# Revit family: LW3-168 MT
name_source: partatom
category: Generic Models
units: mm (PartAtom-declared; Revit-internal decimal feet)

## family parameters
Can host rebar = No
Cut with Voids When Loaded = No
Host = Face
Part Type = Normal
Room Calculation Point = No
Round Connector Dimension = Use Diameter
Shared = No

## types (1)
- LW3-168 MT
    Category = ผนัง
    Default Elevation = 1219 mm
    Depth(mm) = 28 mm  [stored 0.0918635 ft]
    Length(mm) = 2800 mm  [stored 9.18635 ft]
    Material = Teak
    Material main = WPC
    No. of pc / sq.m. = 2.43
    Product Type = ไม้ผนังภายนอก (Cladding Outdoor)
    Product code = LW3-168 MT
    Series = ไม้ผนัง ลักซูรี่ ผิวเคลือบ (Cladding Luxury EU)
    Sub-Category = ไม้ผนัง
    Weight/Sheet (kg) = 7.6
    Width(mm) = 168 mm  [stored 0.551181 ft]

note: [stored X ft] marks values corroborated as IEEE doubles in the binary element streams (Revit-internal decimal feet)

## geometry (parser evidence)
native form markers: Sweep x2
no freeform markers — native parametric forms only
